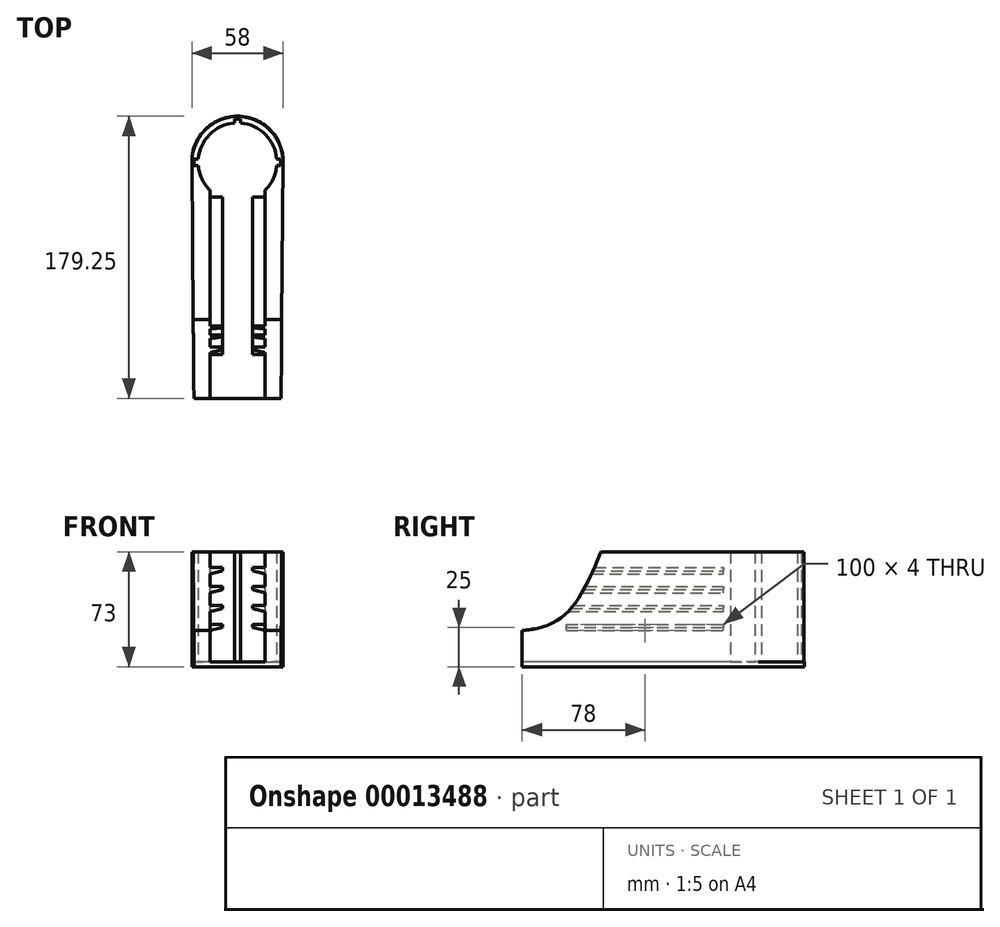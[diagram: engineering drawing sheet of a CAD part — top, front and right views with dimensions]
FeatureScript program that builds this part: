
annotation { "Feature Type Name" : "Feature", "Feature Type Description" : "" }
export const myFeature = defineFeature(function(context is Context, id is Id, definition is map)
    precondition{}
    {
        {
            var Q0;
            Q0=qCreatedBy(makeId("Top.planeOp"),FACE);
            var sketch = newSketch(context, id + "F0", { "sketchPlane" : qUnion([Q0])});
            skArc(sketch, "E0", {"start": v(-24.92, -2) * mm, "mid": v(-22.64, -10.6) * mm, "end": v(-17.5, -17.85) * mm});
            skArc(sketch, "E1", {"start": v(29, 0) * mm, "mid": v(0, 29) * mm, "end": v(-29, 0) * mm});
            skLineSegment(sketch, "E2.rect.bottom", {"start": v(-27.5, 2) * mm, "end": v(-24.92, 2) * mm});
            skLineSegment(sketch, "E2.rect.top", {"start": v(-27.5, -2) * mm, "end": v(-24.92, -2) * mm});
            skLineSegment(sketch, "E2.rect.left", {"start": v(-27.5, 2) * mm, "end": v(-27.5, -2) * mm});
            skLineSegment(sketch, "E2.rect.right", {"start": v(27.5, 2) * mm, "end": v(27.5, -2) * mm});
            skLineSegment(sketch, "E3.rect.bottom", {"start": v(-2, 27.5) * mm, "end": v(2, 27.5) * mm});
            skLineSegment(sketch, "E3.rect.left", {"start": v(-2, 27.5) * mm, "end": v(-2, 24.92) * mm});
            skLineSegment(sketch, "E3.rect.right", {"start": v(2, 27.5) * mm, "end": v(2, 24.92) * mm});
            skLineSegment(sketch, "E4.trimOffspring", {"start": v(24.92, 2) * mm, "end": v(27.5, 2) * mm});
            skLineSegment(sketch, "E5.trimOffspring", {"start": v(24.92, -2) * mm, "end": v(27.5, -2) * mm});
            skArc(sketch, "E6.trimOffspring", {"start": v(24.92, 2) * mm, "mid": v(17.68, 17.68) * mm, "end": v(2, 24.92) * mm});
            skArc(sketch, "E7.trimOffspring", {"start": v(-2, 24.92) * mm, "mid": v(-17.68, 17.68) * mm, "end": v(-24.92, 2) * mm});
            skLineSegment(sketch, "E8", {"start": v(-17.5, 0) * mm, "end": v(17.5, 0) * mm, "construction": true});
            skLineSegment(sketch, "E9", {"start": v(-17.5, 0) * mm, "end": v(-27.5, 0) * mm, "construction": true});
            skLineSegment(sketch, "E10", {"start": v(17.5, 0) * mm, "end": v(27.5, 0) * mm, "construction": true});
            skLineSegment(sketch, "E11", {"start": v(-17.5, 0) * mm, "end": v(-17.5, -23.12) * mm, "construction": true});
            skLineSegment(sketch, "E12", {"start": v(17.5, 0) * mm, "end": v(17.5, -23.12) * mm, "construction": true});
            skLineSegment(sketch, "E13", {"start": v(-29, 0) * mm, "end": v(-27.5, -172.6) * mm});
            skLineSegment(sketch, "E14", {"start": v(29, 0) * mm, "end": v(27.5, -172.6) * mm});
            skLineSegment(sketch, "E15", {"start": v(-27.5, -172.6) * mm, "end": v(-27.5, -172.6) * mm});
            skArc(sketch, "E16", {"start": v(-27.5, -172.6) * mm, "mid": v(0, -200.1) * mm, "end": v(27.5, -172.6) * mm});
            skLineSegment(sketch, "E17.trimOffspring", {"start": v(27.5, -172.6) * mm, "end": v(27.5, -172.6) * mm});
            skLineSegment(sketch, "E18.top", {"start": v(17.5, -172.6) * mm, "end": v(-17.5, -172.6) * mm});
            skLineSegment(sketch, "E18.left", {"start": v(17.5, -23.12) * mm, "end": v(17.5, -172.6) * mm});
            skLineSegment(sketch, "E18.right", {"start": v(-17.5, -23.12) * mm, "end": v(-17.5, -172.6) * mm});
            skArc(sketch, "E19", {"start": v(-17.5, -172.6) * mm, "mid": v(0, -190.1) * mm, "end": v(17.5, -172.6) * mm});
            skArc(sketch, "E20.trimOffspring", {"start": v(17.5, -17.85) * mm, "mid": v(22.64, -10.6) * mm, "end": v(24.92, -2) * mm});
            skLineSegment(sketch, "E21", {"start": v(17.5, -23.12) * mm, "end": v(17.5, -17.85) * mm});
            skLineSegment(sketch, "E22", {"start": v(-17.5, -23.12) * mm, "end": v(-17.5, -17.85) * mm});
            skSolve(sketch);
        }
        {
            var Q0;
            Q0 = qSketchRegion(id + "F0", true);
            extrude(context, id + "F1", {"entities" : qUnion([Q0]), "depth" : 70 * mm});
        }
        {
            var Q0;
            Q0=qCreatedBy(makeId("Front.planeOp"),FACE);
            cPlane(context, id + "F2", {"entities" : qUnion([Q0]), "cplaneType" : CPlaneType.OFFSET, "offset" : 22 * mm, "width" : 150 * mm, "height" : 150 * mm});
        }
        {
            var Q0;
            Q0=qCreatedBy(id+"F2.planeOp",FACE);
            var sketch = newSketch(context, id + "F3", { "sketchPlane" : qUnion([Q0])});
            skLineSegment(sketch, "E23.top", {"start": v(17.5, 24) * mm, "end": v(9.5, 24) * mm});
            skLineSegment(sketch, "E23.left", {"start": v(17.5, 20) * mm, "end": v(17.5, 24) * mm});
            skLineSegment(sketch, "E24", {"start": v(9.5, 24) * mm, "end": v(9.5, 22) * mm});
            skLineSegment(sketch, "E25", {"start": v(17.5, 20) * mm, "end": v(9.5, 22) * mm});
            skLineSegment(sketch, "E26", {"start": v(0, 0) * mm, "end": v(0, 72.92) * mm, "construction": true});
            skLineSegment(sketch, "E27.MirrorCS", {"start": v(-9.5, 24) * mm, "end": v(-9.5, 22) * mm});
            skLineSegment(sketch, "E28.MirrorCS", {"start": v(-17.5, 20) * mm, "end": v(-17.5, 24) * mm});
            skLineSegment(sketch, "E29.MirrorCS", {"start": v(-17.5, 24) * mm, "end": v(-9.5, 24) * mm});
            skLineSegment(sketch, "E30.MirrorCS", {"start": v(-17.5, 20) * mm, "end": v(-9.5, 22) * mm});
            skLineSegment(sketch, "E31.0.1.0", {"start": v(-17.5, 32) * mm, "end": v(-17.5, 36) * mm});
            skLineSegment(sketch, "E31.0.1.1", {"start": v(17.5, 32) * mm, "end": v(9.5, 34) * mm});
            skLineSegment(sketch, "E31.0.1.2", {"start": v(17.5, 32) * mm, "end": v(17.5, 36) * mm});
            skLineSegment(sketch, "E31.0.1.3", {"start": v(-17.5, 32) * mm, "end": v(-9.5, 34) * mm});
            skLineSegment(sketch, "E31.0.1.4", {"start": v(-17.5, 36) * mm, "end": v(-9.5, 36) * mm});
            skLineSegment(sketch, "E31.0.1.5", {"start": v(17.5, 36) * mm, "end": v(9.5, 36) * mm});
            skLineSegment(sketch, "E31.0.1.6", {"start": v(-9.5, 36) * mm, "end": v(-9.5, 34) * mm});
            skLineSegment(sketch, "E31.0.1.7", {"start": v(9.5, 36) * mm, "end": v(9.5, 34) * mm});
            skLineSegment(sketch, "E31.0.2.0", {"start": v(-17.5, 44) * mm, "end": v(-17.5, 48) * mm});
            skLineSegment(sketch, "E31.0.2.1", {"start": v(17.5, 44) * mm, "end": v(9.5, 46) * mm});
            skLineSegment(sketch, "E31.0.2.2", {"start": v(17.5, 44) * mm, "end": v(17.5, 48) * mm});
            skLineSegment(sketch, "E31.0.2.3", {"start": v(-17.5, 44) * mm, "end": v(-9.5, 46) * mm});
            skLineSegment(sketch, "E31.0.2.4", {"start": v(-17.5, 48) * mm, "end": v(-9.5, 48) * mm});
            skLineSegment(sketch, "E31.0.2.5", {"start": v(17.5, 48) * mm, "end": v(9.5, 48) * mm});
            skLineSegment(sketch, "E31.0.2.6", {"start": v(-9.5, 48) * mm, "end": v(-9.5, 46) * mm});
            skLineSegment(sketch, "E31.0.2.7", {"start": v(9.5, 48) * mm, "end": v(9.5, 46) * mm});
            skLineSegment(sketch, "E31.0.3.0", {"start": v(-17.5, 56) * mm, "end": v(-17.5, 60) * mm});
            skLineSegment(sketch, "E31.0.3.1", {"start": v(17.5, 56) * mm, "end": v(9.5, 58) * mm});
            skLineSegment(sketch, "E31.0.3.2", {"start": v(17.5, 56) * mm, "end": v(17.5, 60) * mm});
            skLineSegment(sketch, "E31.0.3.3", {"start": v(-17.5, 56) * mm, "end": v(-9.5, 58) * mm});
            skLineSegment(sketch, "E31.0.3.4", {"start": v(-17.5, 60) * mm, "end": v(-9.5, 60) * mm});
            skLineSegment(sketch, "E31.0.3.5", {"start": v(17.5, 60) * mm, "end": v(9.5, 60) * mm});
            skLineSegment(sketch, "E31.0.3.6", {"start": v(-9.5, 60) * mm, "end": v(-9.5, 58) * mm});
            skLineSegment(sketch, "E31.0.3.7", {"start": v(9.5, 60) * mm, "end": v(9.5, 58) * mm});
            skLineSegment(sketch, "E31.direction1", {"start": v(-17.5, 20) * mm, "end": v(7.5, 20) * mm, "construction": true});
            skLineSegment(sketch, "E31.direction2", {"start": v(-17.5, 20) * mm, "end": v(-17.5, 32) * mm, "construction": true});
            skSolve(sketch);
        }
        {
            var Q0;
            Q0 = qSketchRegion(id + "F3", true);
            extrude(context, id + "F4", {"entities" : qUnion([Q0]), "operationType" : NewBodyOperationType.ADD, "depth" : 100 * mm});
        }
        {
            var Q0;
            Q0=qCreatedBy(makeId("Right.planeOp"),FACE);
            var sketch = newSketch(context, id + "F5", { "sketchPlane" : qUnion([Q0])});
            skLineSegment(sketch, "E32", {"start": v(0, 70) * mm, "end": v(-100, 70) * mm});
            skPoint(sketch, "E33", {"position": v(-200.61, 0) * mm});
            skPoint(sketch, "E34", {"position": v(-200.61, 20) * mm});
            skPoint(sketch, "E35", {"position": v(-172.6, 19.9) * mm});
            skFitSpline(sketch, "E36", {"points": [v(-100, 70) * mm, v(-128.41, 26.04) * mm, v(-172.6, 19.9) * mm, v(-200.61, 20) * mm], "startDerivative": vector(-59.05, -142.9) * mm, "endDerivative": vector(-92.67, -0.98) * mm});
            skSolve(sketch);
        }
        {
            var Q0;
            Q0=qCreatedBy(makeId("Front.planeOp"),FACE);
            var sketch = newSketch(context, id + "F6", { "sketchPlane" : qUnion([Q0])});
            skLineSegment(sketch, "E37.bottom", {"start": v(0, 70) * mm, "end": v(-35.58, 70) * mm});
            skLineSegment(sketch, "E37.top", {"start": v(0, 145) * mm, "end": v(-35.58, 145) * mm});
            skLineSegment(sketch, "E37.right", {"start": v(-35.58, 70) * mm, "end": v(-35.58, 145) * mm});
            skLineSegment(sketch, "E38.bottom", {"start": v(0, 145) * mm, "end": v(39.55, 145) * mm});
            skLineSegment(sketch, "E38.top", {"start": v(0, 70) * mm, "end": v(39.55, 70) * mm});
            skLineSegment(sketch, "E38.left", {"start": v(0, 145) * mm, "end": v(0, 70) * mm});
            skLineSegment(sketch, "E38.right", {"start": v(39.55, 145) * mm, "end": v(39.55, 70) * mm});
            skSolve(sketch);
        }
        {
            var Q0;
            Q0 = qSketchRegion(id + "F6", true);
            var Q1;
            Q1 = qConstructionFilter(qBodyType(qCreatedBy(id + "F5" ,EDGE), BodyType.WIRE), ConstructionObject.NO);
            sweep(context, id + "F7", {"operationType" : NewBodyOperationType.REMOVE, "profiles" : qUnion([Q0]), "path" : qUnion([Q1]), "keepProfileOrientation" : true});
        }
        {
            var Q0;
            Q0=makeQuery(id+"F1.opExtrude","CAP_FACE",FACE,{"disambiguationData":[OSD([sQuery(id+"F0.wireOp",EDGE,"E0"),sQuery(id+"F0.wireOp",EDGE,"E1"),sQuery(id+"F0.wireOp",EDGE,"E2.rect.bottom"),sQuery(id+"F0.wireOp",EDGE,"E2.rect.top"),sQuery(id+"F0.wireOp",EDGE,"E2.rect.left"),sQuery(id+"F0.wireOp",EDGE,"E2.rect.right"),sQuery(id+"F0.wireOp",EDGE,"E3.rect.bottom"),sQuery(id+"F0.wireOp",EDGE,"E3.rect.left"),sQuery(id+"F0.wireOp",EDGE,"E3.rect.right"),sQuery(id+"F0.wireOp",EDGE,"E4.trimOffspring"),sQuery(id+"F0.wireOp",EDGE,"E5.trimOffspring"),sQuery(id+"F0.wireOp",EDGE,"E6.trimOffspring"),sQuery(id+"F0.wireOp",EDGE,"E7.trimOffspring"),sQuery(id+"F0.wireOp",EDGE,"E13"),sQuery(id+"F0.wireOp",EDGE,"E14"),sQuery(id+"F0.wireOp",EDGE,"E15"),sQuery(id+"F0.wireOp",EDGE,"E16"),sQuery(id+"F0.wireOp",EDGE,"E17.trimOffspring"),sQuery(id+"F0.wireOp",EDGE,"E18.left"),sQuery(id+"F0.wireOp",EDGE,"E18.right"),sQuery(id+"F0.wireOp",EDGE,"E19"),sQuery(id+"F0.wireOp",EDGE,"E20.trimOffspring"),sQuery(id+"F0.wireOp",EDGE,"E21"),sQuery(id+"F0.wireOp",EDGE,"E22")])],"isStart":true});
            var sketch = newSketch(context, id + "F8", { "sketchPlane" : qUnion([Q0])});
            skLineSegment(sketch, "E39", {"start": v(-27.5, 172.6) * mm, "end": v(-29, 0) * mm});
            skLineSegment(sketch, "E40", {"start": v(29, 0) * mm, "end": v(27.5, 172.6) * mm});
            skArc(sketch, "E41", {"start": v(27.5, 172.6) * mm, "mid": v(0, 199.87) * mm, "end": v(-27.5, 172.6) * mm});
            skArc(sketch, "E42", {"start": v(-29, 0) * mm, "mid": v(0, -29.25) * mm, "end": v(29, 0) * mm});
            skSolve(sketch);
        }
        {
            var Q0;
            Q0 = qSketchRegion(id + "F8", true);
            extrude(context, id + "F9", {"entities" : qUnion([Q0]), "operationType" : NewBodyOperationType.ADD, "depth" : 3 * mm});
        }
        {
            var Q0;
            Q0=qCreatedBy(makeId("Front.planeOp"),FACE);
            cPlane(context, id + "F10", {"entities" : qUnion([Q0]), "cplaneType" : CPlaneType.OFFSET, "offset" : 150 * mm, "width" : 150 * mm, "height" : 150 * mm});
        }
        {
            var Q0;
            Q0=qCreatedBy(id+"F10.planeOp",FACE);
            var sketch = newSketch(context, id + "F11", { "sketchPlane" : qUnion([Q0])});
            skLineSegment(sketch, "E43.bottom", {"start": v(-48.45, 46.2) * mm, "end": v(43.03, 46.2) * mm});
            skLineSegment(sketch, "E43.top", {"start": v(-48.45, -21.22) * mm, "end": v(43.03, -21.22) * mm});
            skLineSegment(sketch, "E43.left", {"start": v(-48.45, 46.2) * mm, "end": v(-48.45, -21.22) * mm});
            skLineSegment(sketch, "E43.right", {"start": v(43.03, 46.2) * mm, "end": v(43.03, -21.22) * mm});
            skSolve(sketch);
        }
        {
            var Q0;
            Q0 = qSketchRegion(id + "F11", true);
            extrude(context, id + "F12", {"entities" : qUnion([Q0]), "operationType" : NewBodyOperationType.REMOVE, "endBound" : BoundingType.THROUGH_ALL, "depth" : 25 * mm});
        }
    });
